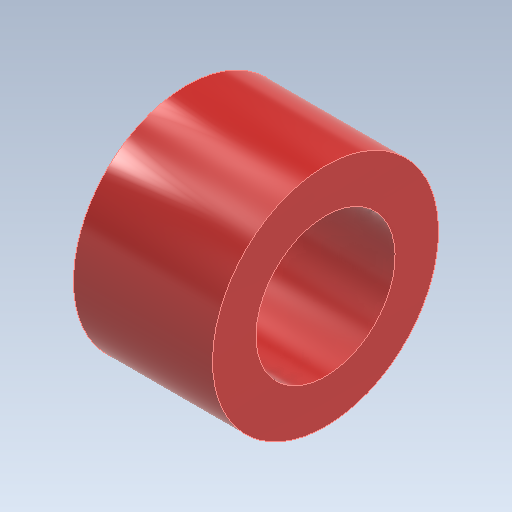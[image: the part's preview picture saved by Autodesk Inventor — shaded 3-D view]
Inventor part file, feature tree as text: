
AUTODESK INVENTOR PART (.ipt)
format: ipt  version: 2021 (Build 250183000, 183)  size: 131,072 bytes
history: native  units: in
note: dims shown in document units (in); Inventor stores cm internally (conversion verified against a paired STEP export)
features: extrude x1, sketch x1
ambient origin geometry x8: Origin, YZ Plane, XZ Plane, XY Plane, X Axis, Y Axis, Z Axis, Center Point
bodies: Solid1 (feature_tree)
feature tree (2):
  extrude  "Extrusion1"  Depth=0.6299in
  sketch  "Sketch1"  dims[d0=0.6299in d1=1.0236in d2=0.6299in d3=0.0in]
